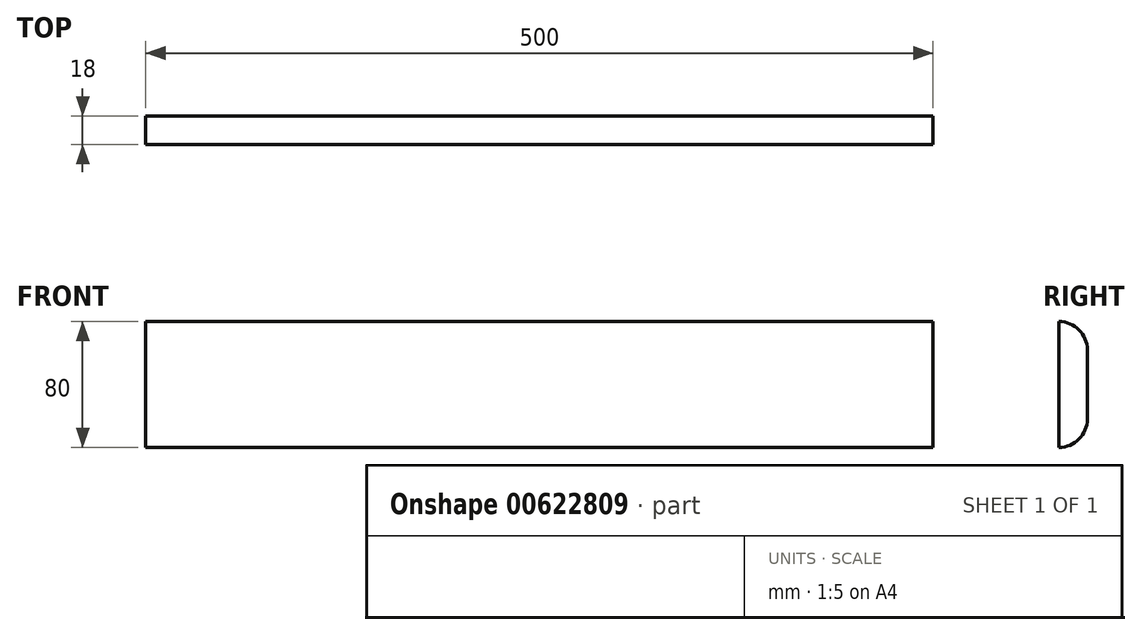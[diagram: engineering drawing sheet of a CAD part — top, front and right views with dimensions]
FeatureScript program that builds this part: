
annotation { "Feature Type Name" : "Feature", "Feature Type Description" : "" }
export const myFeature = defineFeature(function(context is Context, id is Id, definition is map)
    precondition{}
    {
        {
            var Q0;
            Q0=qCreatedBy(makeId("Front.planeOp"),FACE);
            var sketch = newSketch(context, id + "F0", { "sketchPlane" : qUnion([Q0])});
            skLineSegment(sketch, "E0.bottom", {"start": v(298.92, 1.82) * mm, "end": v(-201.08, 1.82) * mm});
            skLineSegment(sketch, "E0.top", {"start": v(298.92, -78.18) * mm, "end": v(-201.08, -78.18) * mm});
            skLineSegment(sketch, "E0.left", {"start": v(298.92, 1.82) * mm, "end": v(298.92, -78.18) * mm});
            skLineSegment(sketch, "E0.right", {"start": v(-201.08, 1.82) * mm, "end": v(-201.08, -78.18) * mm});
            skSolve(sketch);
        }
        {
            var Q0;
            Q0 = qSketchRegion(id + "F0", true);
            extrude(context, id + "F1", {"entities" : qUnion([Q0]), "depth" : 18 * mm, "offsetDistance" : 25 * mm});
        }
        {
            var Q0;
            Q0=makeQuery(id+"F1.opExtrude","CAP_EDGE",EDGE,{"disambiguationData":[OSD([sQuery(id+"F0.wireOp",EDGE,"E0.top")])],"isStart":true});
            var Q1;
            Q1=makeQuery(id+"F1.opExtrude","CAP_EDGE",EDGE,{"disambiguationData":[OSD([sQuery(id+"F0.wireOp",EDGE,"E0.bottom")])],"isStart":true});
            fillet(context, id + "F2", {"entities" : qUnion([Q0, Q1]), "radius" : 18 * mm, "tangentPropagation" : true, "allowEdgeOverflow" : false});
        }
    });
